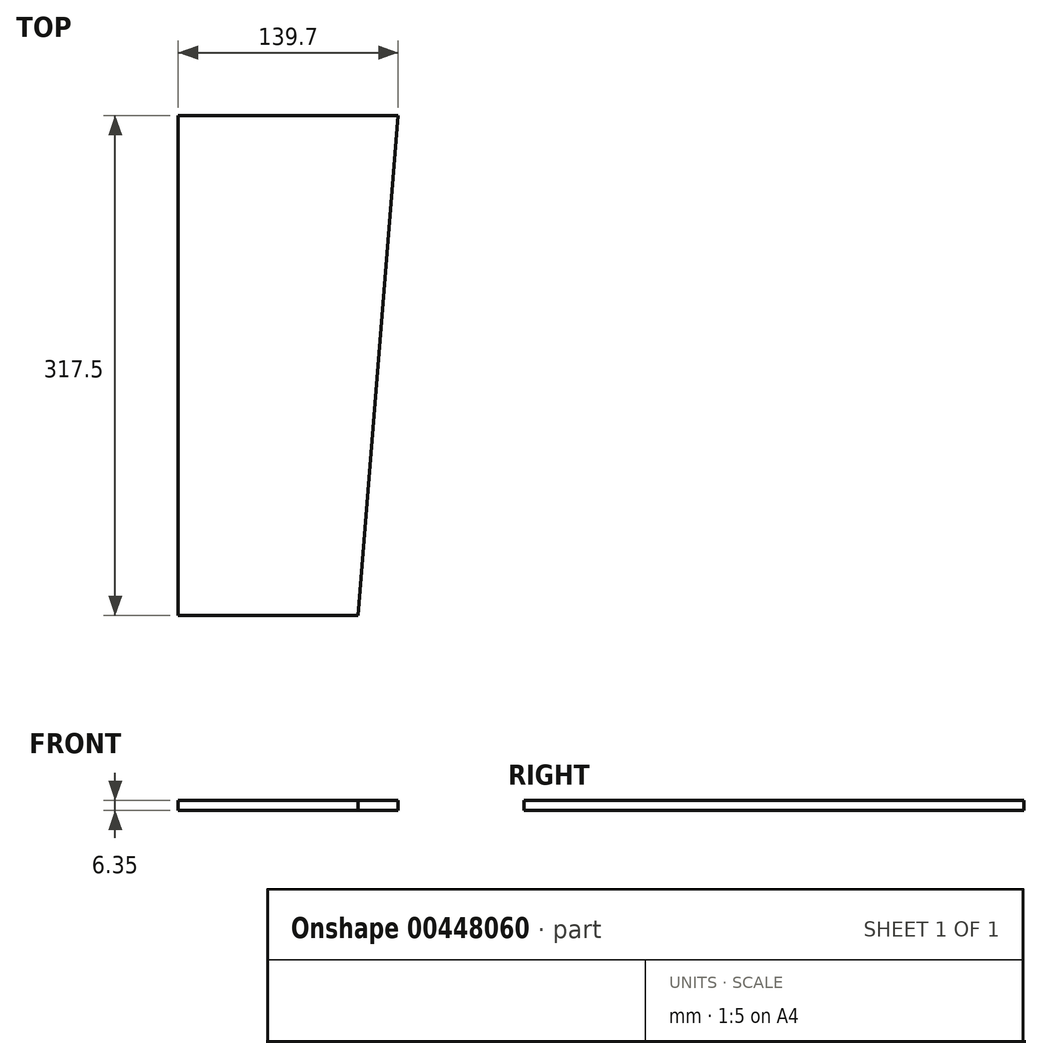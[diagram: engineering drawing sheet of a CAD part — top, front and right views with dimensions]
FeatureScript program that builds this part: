
annotation { "Feature Type Name" : "Feature", "Feature Type Description" : "" }
export const myFeature = defineFeature(function(context is Context, id is Id, definition is map)
    precondition{}
    {
        {
            var Q0;
            Q0=qCreatedBy(makeId("Top.planeOp"),FACE);
            var sketch = newSketch(context, id + "F0", { "sketchPlane" : qUnion([Q0])});
            skLineSegment(sketch, "E0", {"start": v(0, 180.18) * mm, "end": v(0, -137.32) * mm});
            skLineSegment(sketch, "E1", {"start": v(0, 180.18) * mm, "end": v(139.7, 180.18) * mm});
            skLineSegment(sketch, "E2", {"start": v(0, -137.32) * mm, "end": v(114.3, -137.32) * mm});
            skLineSegment(sketch, "E3", {"start": v(114.3, -137.32) * mm, "end": v(139.7, 180.18) * mm});
            skPoint(sketch, "E4", {"position": v(50.8, 180.18) * mm});
            skLineSegment(sketch, "E5", {"start": v(50.8, 180.18) * mm, "end": v(50.8, 268.16) * mm});
            skLineSegment(sketch, "E6", {"start": v(50.8, 268.16) * mm, "end": v(0, 180.18) * mm});
            skSolve(sketch);
        }
        {
            var Q0;
            {var subQ3=sQuery(id+"F0.wireOp",EDGE,"E0");Q0=makeQuery(id+"F0.imprint","IMPRINT",FACE,{"disambiguationData":[TD([[makeQuery(id+"F0.imprint","IMPRINT",EDGE,{"derivedFrom":subQ3}),1.0]])]});}
            extrude(context, id + "F1", {"entities" : qUnion([Q0]), "depth" : 6.35 * mm});
        }
    });
